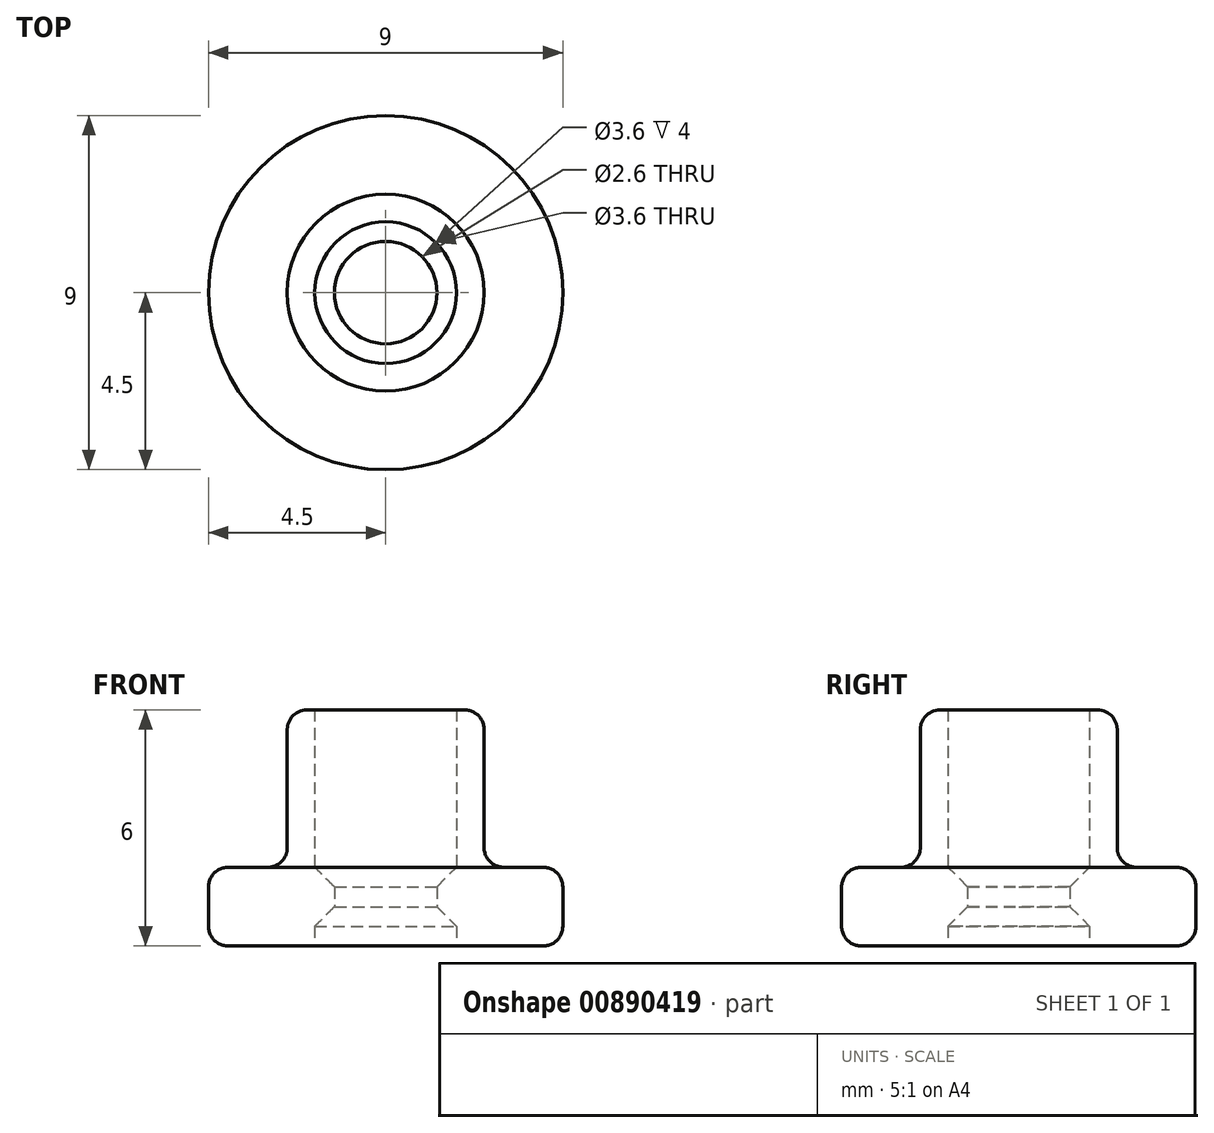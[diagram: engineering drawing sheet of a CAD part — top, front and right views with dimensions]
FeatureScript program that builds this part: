
annotation { "Feature Type Name" : "Feature", "Feature Type Description" : "" }
export const myFeature = defineFeature(function(context is Context, id is Id, definition is map)
    precondition{}
    {
        {
            var Q0;
            Q0=qCreatedBy(makeId("Front.planeOp"),FACE);
            var sketch = newSketch(context, id + "F0", { "sketchPlane" : qUnion([Q0])});
            skLineSegment(sketch, "E0", {"start": v(0, 0) * mm, "end": v(4.5, 0) * mm});
            skLineSegment(sketch, "E1", {"start": v(4.5, 0) * mm, "end": v(4.5, 2) * mm});
            skLineSegment(sketch, "E2", {"start": v(4.5, 2) * mm, "end": v(1.8, 2) * mm});
            skLineSegment(sketch, "E3", {"start": v(1.8, 0) * mm, "end": v(1.8, 0.5) * mm});
            skLineSegment(sketch, "E4", {"start": v(1.8, 0.5) * mm, "end": v(1.3, 1) * mm});
            skLineSegment(sketch, "E5", {"start": v(1.3, 1) * mm, "end": v(1.3, 1.5) * mm});
            skLineSegment(sketch, "E6", {"start": v(1.3, 1.5) * mm, "end": v(1.8, 2) * mm});
            skLineSegment(sketch, "E7", {"start": v(2.5, 2) * mm, "end": v(2.5, 6) * mm});
            skLineSegment(sketch, "E8", {"start": v(1.8, 2) * mm, "end": v(1.8, 6) * mm});
            skLineSegment(sketch, "E9", {"start": v(2.5, 6) * mm, "end": v(0, 6) * mm});
            skLineSegment(sketch, "E10", {"start": v(0, 0) * mm, "end": v(0, 6) * mm, "construction": true});
            skSolve(sketch);
        }
        {
            var Q0;
            Q0 = qSketchRegion(id + "F0", true);
            var Q1;
            Q1=sQuery(id+"F0.wireOp",EDGE,"E10");
            revolve(context, id + "F1", {"surfaceOperationType" : NewSurfaceOperationType.NEW, "entities" : qUnion([Q0]), "axis" : qUnion([Q1]), "revolveType" : RevolveType.FULL});
        }
        {
            var Q0;
            Q0=makeQuery(id+"F1.opRevolve","SWEPT_EDGE",EDGE,{"disambiguationData":[OSD([sQuery(id+"F0.wireOp",EDGE,"E7"),sQuery(id+"F0.wireOp",EDGE,"E9")])]});
            var Q1;
            Q1=makeQuery(id+"F1.opRevolve","SWEPT_FACE",FACE,{"disambiguationData":[OSD([sQuery(id+"F0.wireOp",EDGE,"E2")])]});
            var Q2;
            Q2=makeQuery(id+"F1.opRevolve","SWEPT_EDGE",EDGE,{"disambiguationData":[OSD([sQuery(id+"F0.wireOp",EDGE,"E0"),sQuery(id+"F0.wireOp",EDGE,"E1")])]});
            fillet(context, id + "F2", {"entities" : qUnion([Q0, Q1, Q2]), "radius" : 0.5 * mm, "tangentPropagation" : true, "allowEdgeOverflow" : false});
        }
    });
